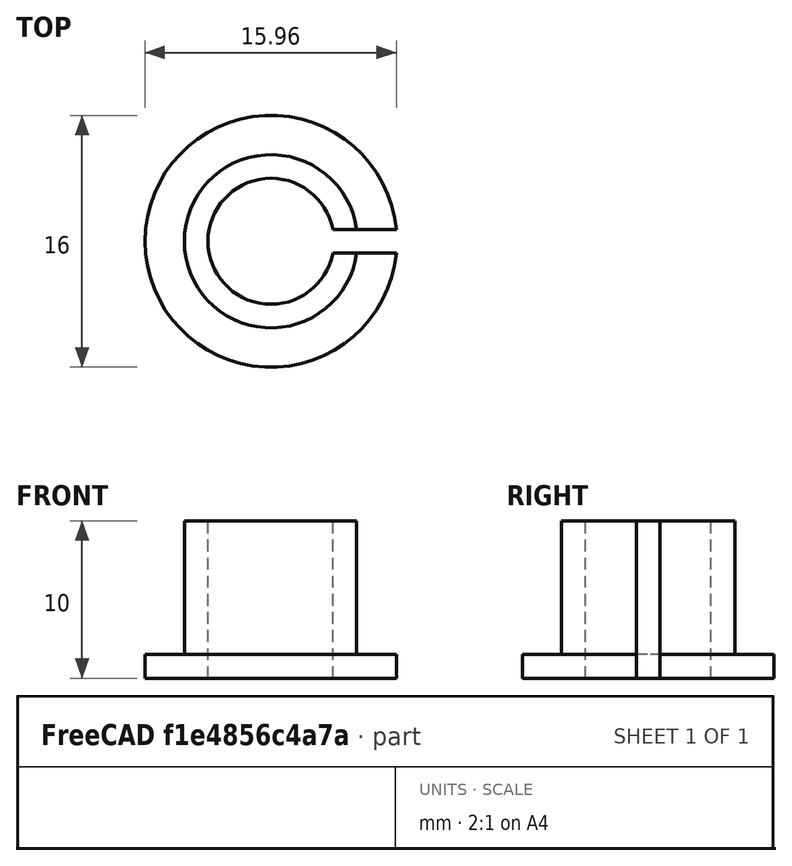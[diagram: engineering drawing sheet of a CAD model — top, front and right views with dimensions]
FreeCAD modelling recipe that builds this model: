
FCSTD DOCUMENT  (FreeCAD 0.18R16117 (Git))
Label: gx24-holder
License: CreativeCommons Attribution-ShareAlike
LicenseURL: http://creativecommons.org/licenses/by-sa/4.0/
objects: Part::Cylinder×3, Part::Cut×2, Part::Fuse×1, Part::Box×1
note: 7 computed .brp shape members not serialized (recipe doc carries the construction recipe); baked Part::Feature solids carry a one-line shape summary decoded from their .brp

FEATURE [Part::Cylinder] Cylinder  label="holder"
  Angle = 360
  AttacherType = Attacher::AttachEngine3D
  Height = 10
  Radius = 5.5
FEATURE [Part::Cylinder] Cylinder001  label="base"
  Angle = 360
  AttacherType = Attacher::AttachEngine3D
  Height = 1.5
  Radius = 8
FEATURE [Part::Cylinder] Cylinder002  label="hole"
  Angle = 360
  AttacherType = Attacher::AttachEngine3D
  Height = 15
  Radius = 4
FEATURE [Part::Fuse] Fusion
  Base = -> Cylinder
  Tool = -> Cylinder001
FEATURE [Part::Cut] Cut
  Base = -> Fusion
  Tool = -> Cylinder002
FEATURE [Part::Box] Box  label="Cube"
  AttacherType = Attacher::AttachEngine3D
  Height = 15
  Length = 11
  Placement = pos=(0,-0.75,0) rot=(0,0,1;0rad)
  Width = 1.5
FEATURE [Part::Cut] Cut001
  Base = -> Cut
  Tool = -> Box
